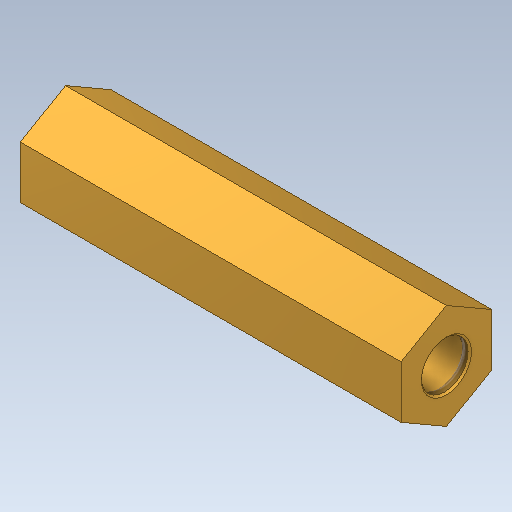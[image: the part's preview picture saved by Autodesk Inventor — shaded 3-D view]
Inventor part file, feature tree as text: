
AUTODESK INVENTOR PART (.ipt)
format: ipt  version: 2021 (Build 250183000, 183)  size: 117,760 bytes
history: native  units: mm
features: other x5, thread x2, revolve x1, chamfer x1
ambient origin geometry x6: Origin, XZ Plane, XY Plane, X Axis, Y Axis, Z Axis
bodies: Solid1 (feature_tree)
feature tree (9):
  revolve  "Revolution1"  [1 undecoded]
  other  "N-Side1"
  thread  "Thread2"  [1 undecoded]
  other  "Start Plane"
  other  "Origin point"
  other  "Main Sketch"
  other  "iFeature1:1"
  thread  "Thread1"  [1 undecoded]
  chamfer  "Chamfer1"  Distance=2.459mm
note: 3 required parameter values undecoded (feature->parameter linkage not recoverable at this tier; creation-order binding heuristic only, values carry confidence <= 0.55)